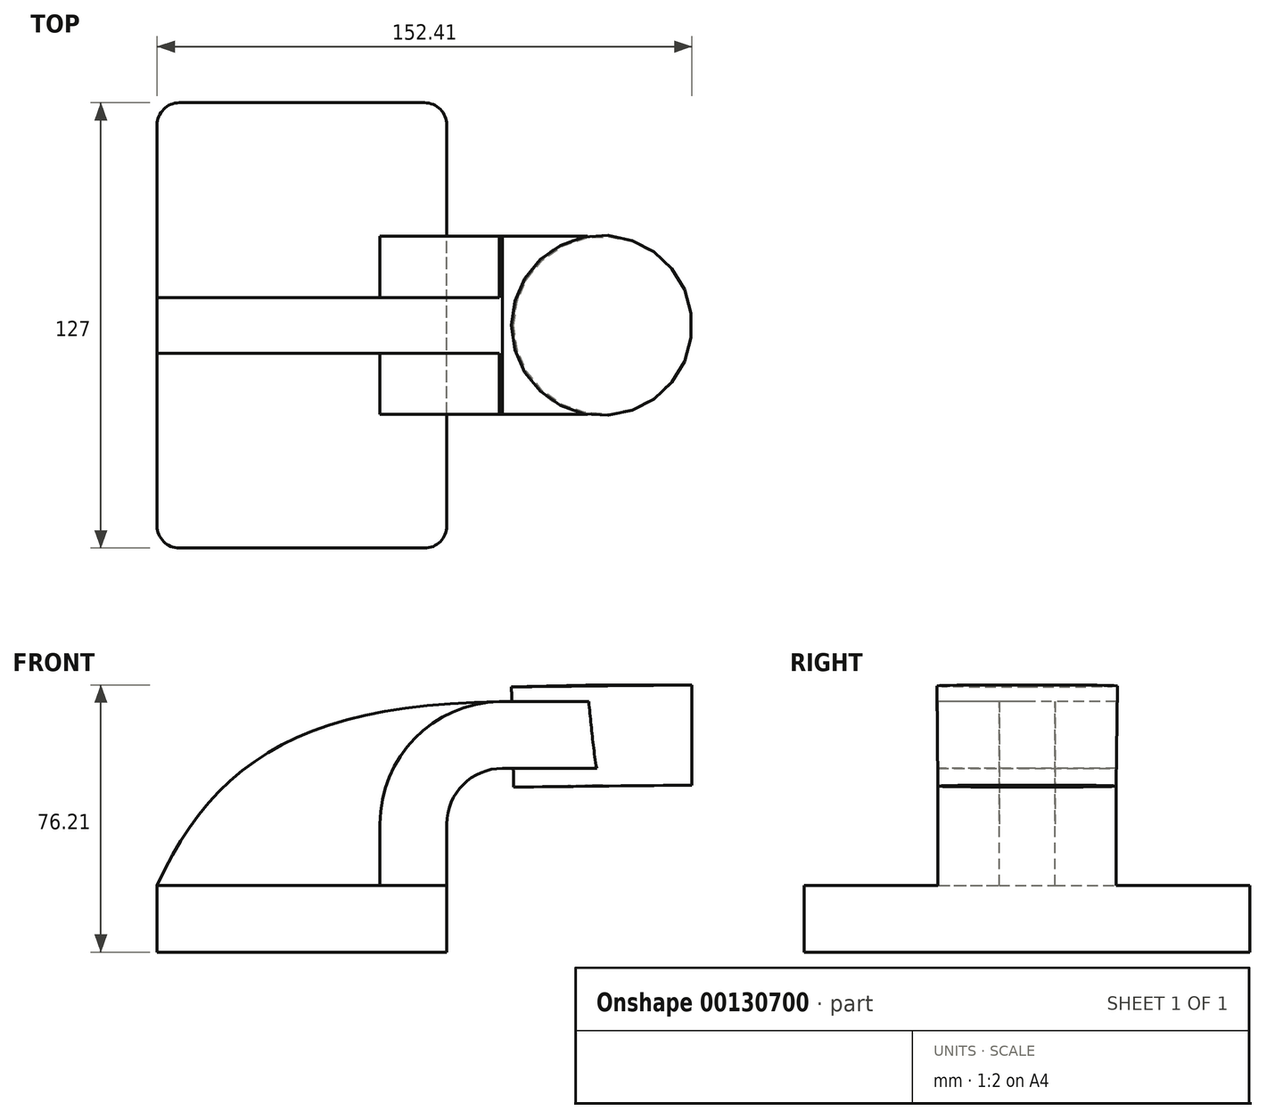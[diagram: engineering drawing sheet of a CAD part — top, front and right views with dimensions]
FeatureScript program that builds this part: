
annotation { "Feature Type Name" : "Feature", "Feature Type Description" : "" }
export const myFeature = defineFeature(function(context is Context, id is Id, definition is map)
    precondition{}
    {
        {
            var Q0;
            Q0=qCreatedBy(makeId("Front.planeOp"),FACE);
            var sketch = newSketch(context, id + "F0", { "sketchPlane" : qUnion([Q0])});
            skLineSegment(sketch, "E0.bottom", {"start": v(-41.28, -9.53) * mm, "end": v(41.28, -9.53) * mm});
            skLineSegment(sketch, "E0.top", {"start": v(-41.28, 9.53) * mm, "end": v(41.28, 9.53) * mm});
            skLineSegment(sketch, "E0.left", {"start": v(-41.28, -9.53) * mm, "end": v(-41.28, 9.53) * mm});
            skLineSegment(sketch, "E0.right", {"start": v(41.28, -9.53) * mm, "end": v(41.28, 9.52) * mm});
            skPoint(sketch, "E0.middle", {"position": v(0, 0) * mm});
            skLineSegment(sketch, "E1.bottom", {"start": v(60.33, 38.1) * mm, "end": v(111.12, 38.1) * mm});
            skLineSegment(sketch, "E1.top", {"start": v(60.32, 66.67) * mm, "end": v(111.12, 66.67) * mm});
            skLineSegment(sketch, "E1.left", {"start": v(60.33, 38.1) * mm, "end": v(60.32, 66.67) * mm});
            skLineSegment(sketch, "E1.right", {"start": v(111.12, 38.1) * mm, "end": v(111.12, 66.67) * mm});
            skPoint(sketch, "E1.middle", {"position": v(85.72, 52.39) * mm});
            skLineSegment(sketch, "E2", {"start": v(41.28, 9.52) * mm, "end": v(41.28, 27) * mm});
            skArc(sketch, "E3", {"start": v(41.27, 27) * mm, "mid": v(45.92, 38.23) * mm, "end": v(57.15, 42.88) * mm});
            skArc(sketch, "E4.1", {"start": v(22.22, 27) * mm, "mid": v(32.45, 51.7) * mm, "end": v(57.15, 61.93) * mm});
            skLineSegment(sketch, "E4.2", {"start": v(22.22, 9.52) * mm, "end": v(22.22, 27) * mm});
            skLineSegment(sketch, "E5", {"start": v(85.72, 38.1) * mm, "end": v(85.4, 66.67) * mm});
            skFitSpline(sketch, "E6", {"points": [v(-41.28, 9.53) * mm, v(57.15, 61.93) * mm], "startDerivative": vector(47.8, 104.74) * mm, "endDerivative": vector(171.45, 1.95) * mm});
            skLineSegment(sketch, "E7", {"start": v(57.15, 42.88) * mm, "end": v(85.67, 42.88) * mm});
            skLineSegment(sketch, "E8.0", {"start": v(57.15, 61.93) * mm, "end": v(85.67, 61.93) * mm});
            skSolve(sketch);
        }
        {
            var Q0;
            Q0=makeQuery(id+"F0.imprint","IMPRINT",FACE,{"disambiguationData":[TD([[makeQuery(id+"F0.imprint","IMPRINT",EDGE,{"derivedFrom":sQuery(id+"F0.wireOp",EDGE,"E0.bottom")}),1.0]])]});
            extrude(context, id + "F1", {"entities" : qUnion([Q0]), "endBound" : BoundingType.SYMMETRIC, "depth" : 127 * mm});
        }
        {
            var Q0;
            {var subQ7=sQuery(id+"F0.wireOp",EDGE,"E2");Q0=makeQuery(id+"F0.imprint","IMPRINT",FACE,{"disambiguationData":[TD([[makeQuery(id+"F0.imprint","IMPRINT",EDGE,{"derivedFrom":subQ7}),1.0]])]});}
            var Q1;
            {var subQ0=sQuery(id+"F0.wireOp",EDGE,"E7");var subQ1=sQuery(id+"F0.wireOp",EDGE,"E1.left");var subQ2=makeQuery(id+"F0.imprint","INTERSECT",VERTEX,{"derivedFrom":[subQ1,subQ0]});Q1=makeQuery(id+"F0.imprint","IMPRINT",FACE,{"disambiguationData":[TD([[makeQuery(id+"F0.imprint","IMPRINT",EDGE,{"disambiguationData":[TD([[subQ2,-1.0]])],"derivedFrom":subQ1}),-1.0]])]});}
            extrude(context, id + "F2", {"entities" : qUnion([Q0, Q1]), "operationType" : NewBodyOperationType.ADD, "endBound" : BoundingType.SYMMETRIC, "depth" : 50.8 * mm});
        }
        {
            var Q0;
            {var subQ3=sQuery(id+"F0.wireOp",EDGE,"E4.2");Q0=makeQuery(id+"F0.imprint","IMPRINT",FACE,{"disambiguationData":[TD([[makeQuery(id+"F0.imprint","IMPRINT",EDGE,{"derivedFrom":subQ3}),1.0]])]});}
            extrude(context, id + "F3", {"entities" : qUnion([Q0]), "operationType" : NewBodyOperationType.ADD, "endBound" : BoundingType.SYMMETRIC, "depth" : 15.88 * mm});
        }
        {
            var Q0;
            {var subQ4=sQuery(id+"F0.wireOp",EDGE,"E1.right");Q0=makeQuery(id+"F0.imprint","IMPRINT",FACE,{"disambiguationData":[TD([[makeQuery(id+"F0.imprint","IMPRINT",EDGE,{"derivedFrom":subQ4}),1.0]])]});}
            var Q1;
            Q1=sQuery(id+"F0.wireOp",EDGE,"E5");
            revolve(context, id + "F4", {"operationType" : NewBodyOperationType.ADD, "entities" : qUnion([Q0]), "axis" : qUnion([Q1]), "revolveType" : RevolveType.FULL});
        }
        {
            var Q0;
            Q0=makeQuery(id+"F1.opExtrude","CAP_EDGE",EDGE,{"disambiguationData":[OSD([sQuery(id+"F0.wireOp",EDGE,"E0.right")])],"isStart":false});
            var Q1;
            Q1=makeQuery(id+"F1.opExtrude","CAP_EDGE",EDGE,{"disambiguationData":[OSD([sQuery(id+"F0.wireOp",EDGE,"E0.left")])],"isStart":false});
            var Q2;
            Q2=makeQuery(id+"F1.opExtrude","CAP_EDGE",EDGE,{"disambiguationData":[OSD([sQuery(id+"F0.wireOp",EDGE,"E0.right")])],"isStart":true});
            var Q3;
            Q3=makeQuery(id+"F1.opExtrude","CAP_EDGE",EDGE,{"disambiguationData":[OSD([sQuery(id+"F0.wireOp",EDGE,"E0.left")])],"isStart":true});
            fillet(context, id + "F5", {"entities" : qUnion([Q0, Q1, Q2, Q3]), "radius" : 6.35 * mm, "tangentPropagation" : true, "allowEdgeOverflow" : false});
        }
    });
